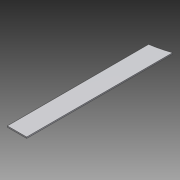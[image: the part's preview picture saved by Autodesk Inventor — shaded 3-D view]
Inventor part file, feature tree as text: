
AUTODESK INVENTOR PART (.ipt)
format: ipt  version: 2014 SP1 (Build 180222100, 222)  size: 74,240 bytes
history: native  units: in
note: dims shown in document units (in); Inventor stores cm internally (conversion verified against a paired STEP export)
features: extrude x1, sketch x1
ambient origin geometry x8: Origin, YZ Plane, XZ Plane, XY Plane, X Axis, Y Axis, Z Axis, Center Point
bodies: Solid1 (feature_tree)
feature tree (2):
  extrude  "Extrusion1"  Depth=0.0625in
  sketch  "Sketch1"  dims[d0=11.5in d1=13.0in d2=13.0in d4=1.0in d8=3.875in d11=0.0625in d12=0.0in]
